# Revit family: AFX-Metropolitan-Pendant
name_source: partatom
category: Lighting Fixtures
units: mm (PartAtom-declared; Revit-internal decimal feet)

## family parameters
Cut with Voids When Loaded = No
Host = Face
Light Source = No
Maintain Annotation Orientation = No
Part Type = Normal
Room Calculation Point = No
Round Connector Dimension = Use Diameter
Shared = No

## types (1)
- METP27
    Apparent Load = 0 VA
    Assembly Code = D5020200
    Canopy Finish = AFX - Paint Black
    Default Elevation = 48"
    Description = LED Pendant - 27" Dia x 21"H
    Diameter = 27"
    Diffuser Finish = AFX - Diffuser
    Height = 21"
    Keynote = 12500
    Manufacturer = AFX Inc
    Model = METP27
    Power Factor = 1
    Product Documentation Link = https://www.afxinc.com
    Revit Model Built By = https://www.servex-us.com
    Support Finish = AFX - Paint Black
    Sustainability = https://lamprecycle.org
    Type Comments = Metropolitan
    URL = https://www.afxinc.com
    Voltage = 120 V
    Wattage Comments = 30W

## geometry (parser evidence)
native form markers: Sweep x4
no freeform markers — native parametric forms only
